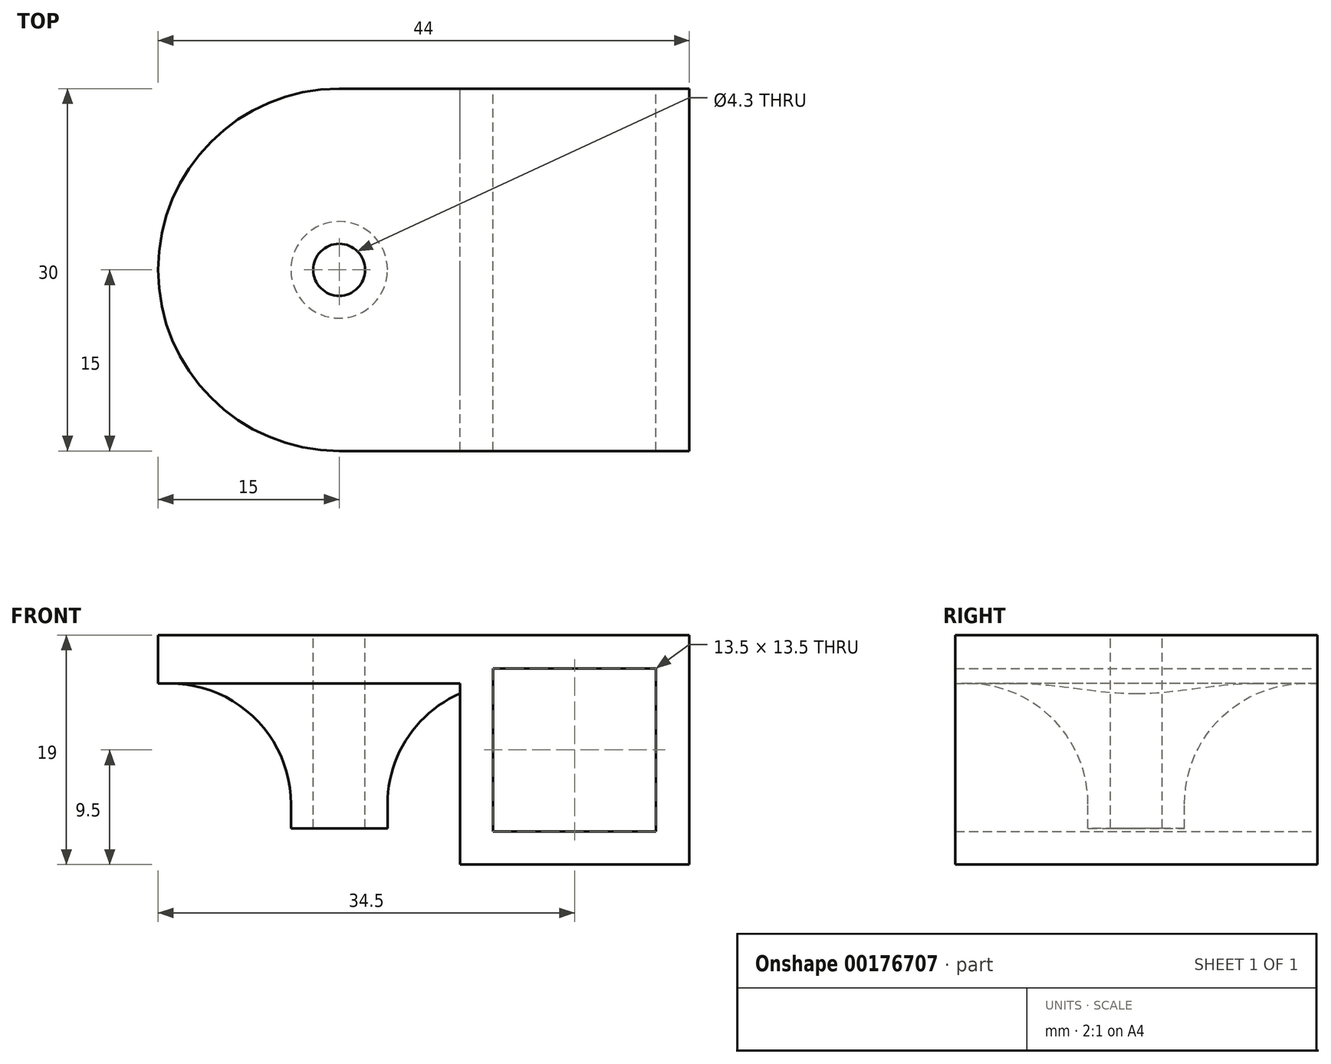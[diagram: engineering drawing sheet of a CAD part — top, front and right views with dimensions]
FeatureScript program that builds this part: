
annotation { "Feature Type Name" : "Feature", "Feature Type Description" : "" }
export const myFeature = defineFeature(function(context is Context, id is Id, definition is map)
    precondition{}
    {
        {
            var Q0;
            Q0=qCreatedBy(makeId("Front.planeOp"),FACE);
            var sketch = newSketch(context, id + "F0", { "sketchPlane" : qUnion([Q0])});
            skLineSegment(sketch, "E0.bottom", {"start": v(9.5, 9.5) * mm, "end": v(-9.5, 9.5) * mm});
            skLineSegment(sketch, "E0.top", {"start": v(9.5, -9.5) * mm, "end": v(-9.5, -9.5) * mm});
            skLineSegment(sketch, "E0.left", {"start": v(9.5, 9.5) * mm, "end": v(9.5, -9.5) * mm});
            skLineSegment(sketch, "E0.right", {"start": v(-9.5, 9.5) * mm, "end": v(-9.5, -9.5) * mm});
            skPoint(sketch, "E0.middle", {"position": v(0, 0) * mm});
            skLineSegment(sketch, "E1.bottom", {"start": v(6.75, 6.75) * mm, "end": v(-6.75, 6.75) * mm});
            skLineSegment(sketch, "E1.top", {"start": v(6.75, -6.75) * mm, "end": v(-6.75, -6.75) * mm});
            skLineSegment(sketch, "E1.left", {"start": v(6.75, 6.75) * mm, "end": v(6.75, -6.75) * mm});
            skLineSegment(sketch, "E1.right", {"start": v(-6.75, 6.75) * mm, "end": v(-6.75, -6.75) * mm});
            skSolve(sketch);
        }
        {
            var Q0;
            Q0=makeQuery(id+"F0.imprint","IMPRINT",FACE,{"disambiguationData":[TD([[makeQuery(id+"F0.imprint","IMPRINT",EDGE,{"derivedFrom":sQuery(id+"F0.wireOp",EDGE,"E0.bottom")}),1.0]])]});
            extrude(context, id + "F1", {"entities" : qUnion([Q0]), "endBound" : BoundingType.SYMMETRIC, "depth" : 30 * mm});
        }
        {
            var Q0;
            Q0=makeQuery(id+"F1.opExtrude","SWEPT_FACE",FACE,{"disambiguationData":[OSD([sQuery(id+"F0.wireOp",EDGE,"E0.bottom")])]});
            var sketch = newSketch(context, id + "F2", { "sketchPlane" : qUnion([Q0])});
            skLineSegment(sketch, "E2", {"start": v(-9.5, 15) * mm, "end": v(-19.5, 15) * mm});
            skLineSegment(sketch, "E3", {"start": v(-9.5, -15) * mm, "end": v(-19.5, -15) * mm});
            skArc(sketch, "E4", {"start": v(-19.5, 15) * mm, "mid": v(-34.5, 0) * mm, "end": v(-19.5, -15) * mm});
            skCircle(sketch, "E5", {"center": v(-19.5, 0) * mm, "radius": 2.15 * mm});
            skCircle(sketch, "E6", {"center": v(-19.5, 0) * mm, "radius": 4 * mm});
            skSolve(sketch);
        }
        {
            var Q0;
            Q0 = qSketchRegion(id + "F2", true);
            var Q1;
            Q1=makeQuery(id+"F2.imprint","IMPRINT",FACE,{"disambiguationData":[TD([[makeQuery(id+"F2.imprint","IMPRINT",EDGE,{"derivedFrom":sQuery(id+"F2.wireOp",EDGE,"E2")}),1.0]])]});
            extrude(context, id + "F3", {"entities" : qUnion([Q0, Q1]), "operationType" : NewBodyOperationType.ADD, "oppositeDirection" : true, "depth" : 4 * mm});
        }
        {
            var Q0;
            Q0=makeQuery(id+"F2.imprint","IMPRINT",FACE,{"disambiguationData":[TD([[makeQuery(id+"F2.imprint","IMPRINT",EDGE,{"derivedFrom":sQuery(id+"F2.wireOp",EDGE,"E5")}),-1.0]])]});
            var Q1;
            Q1=makeQuery(id+"F2.imprint","IMPRINT",FACE,{"disambiguationData":[TD([[makeQuery(id+"F2.imprint","IMPRINT",EDGE,{"derivedFrom":sQuery(id+"F2.wireOp",EDGE,"E6")}),1.0]])]});
            extrude(context, id + "F4", {"entities" : qUnion([Q0, Q1]), "operationType" : NewBodyOperationType.ADD, "oppositeDirection" : true, "depth" : 16 * mm});
        }
        {
            var Q0;
            Q0=makeQuery(id+"F4.boolean.opBoolean","INTERSECT",EDGE,{"derivedFrom":[makeQuery(id+"F3.opExtrude","CAP_FACE",FACE,{"disambiguationData":[OSD([sQuery(id+"F0.wireOp",EDGE,"E0.bottom"),sQuery(id+"F0.wireOp",EDGE,"E0.right"),sQuery(id+"F2.wireOp",EDGE,"E2"),sQuery(id+"F2.wireOp",EDGE,"E3"),sQuery(id+"F2.wireOp",EDGE,"E4"),sQuery(id+"F2.wireOp",EDGE,"E5")])],"isStart":false}),makeQuery(id+"F4.opExtrude","SWEPT_FACE",FACE,{"disambiguationData":[OSD([sQuery(id+"F2.wireOp",EDGE,"E6")])]})]});
            var Q1;
            Q1=makeQuery(id+"F3.opExtrude","CAP_EDGE",EDGE,{"disambiguationData":[OSD([sQuery(id+"F0.wireOp",EDGE,"E0.bottom"),sQuery(id+"F0.wireOp",EDGE,"E0.right")])],"isStart":false});
            fillet(context, id + "F5", {"entities" : qUnion([Q0, Q1]), "radius" : 10 * mm, "tangentPropagation" : true, "allowEdgeOverflow" : false});
        }
    });
